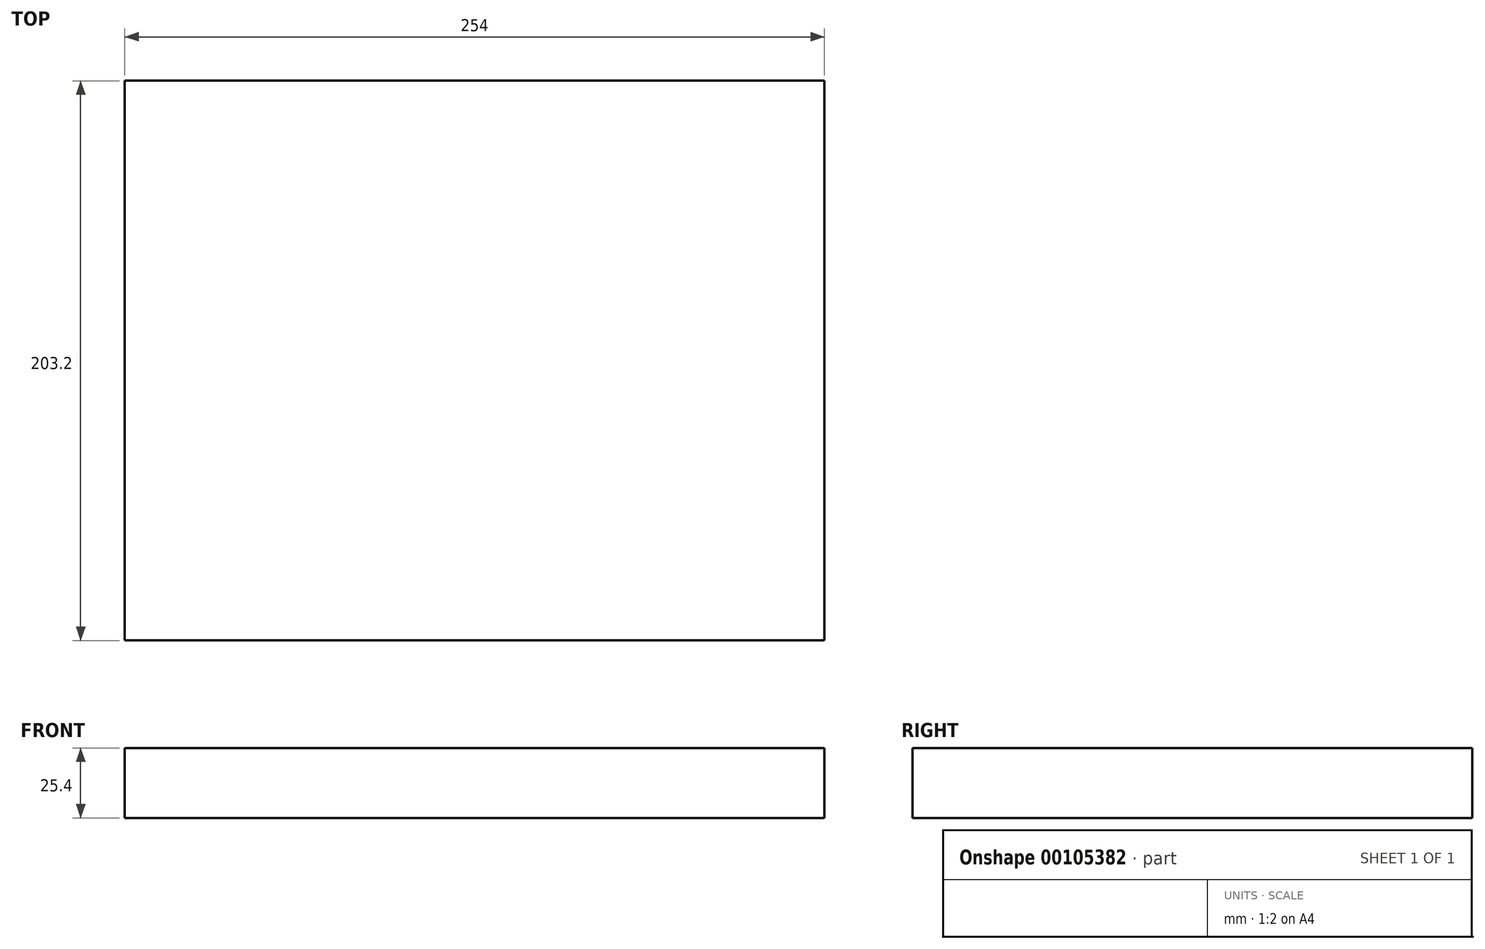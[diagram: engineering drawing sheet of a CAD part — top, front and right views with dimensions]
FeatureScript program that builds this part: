
annotation { "Feature Type Name" : "Feature", "Feature Type Description" : "" }
export const myFeature = defineFeature(function(context is Context, id is Id, definition is map)
    precondition{}
    {
        {
            var Q0;
            Q0=qCreatedBy(makeId("Top.planeOp"),FACE);
            var sketch = newSketch(context, id + "F0", { "sketchPlane" : qUnion([Q0])});
            skLineSegment(sketch, "E0.bottom", {"start": v(-112.1, 141.05) * mm, "end": v(141.9, 141.05) * mm});
            skLineSegment(sketch, "E0.top", {"start": v(-112.1, -62.15) * mm, "end": v(141.9, -62.15) * mm});
            skLineSegment(sketch, "E0.left", {"start": v(-112.1, 141.05) * mm, "end": v(-112.1, -62.15) * mm});
            skLineSegment(sketch, "E0.right", {"start": v(141.9, 141.05) * mm, "end": v(141.9, -62.15) * mm});
            skSolve(sketch);
        }
        {
            var Q0;
            Q0 = qSketchRegion(id + "F0", true);
            extrude(context, id + "F1", {"entities" : qUnion([Q0]), "depth" : 25.4 * mm});
        }
    });
